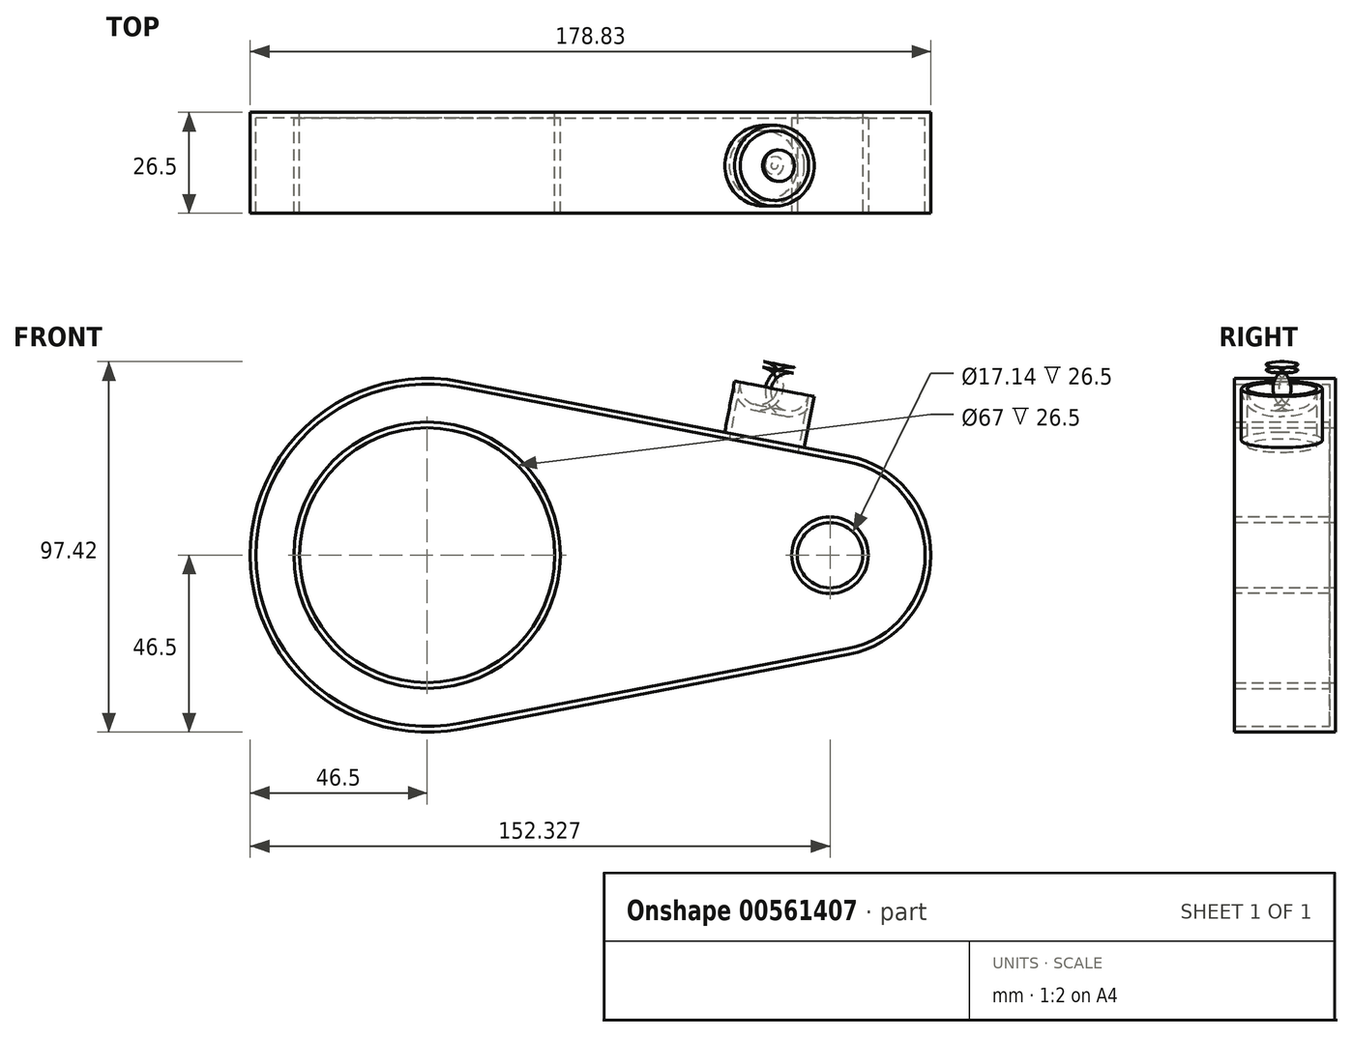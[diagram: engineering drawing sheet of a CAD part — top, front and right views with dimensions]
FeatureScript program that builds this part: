
annotation { "Feature Type Name" : "Feature", "Feature Type Description" : "" }
export const myFeature = defineFeature(function(context is Context, id is Id, definition is map)
    precondition{}
    {
        {
            var Q0;
            Q0=qCreatedBy(makeId("Front.planeOp"),FACE);
            var sketch = newSketch(context, id + "F0", { "sketchPlane" : qUnion([Q0])});
            skCircle(sketch, "E0", {"center": v(0, 0) * mm, "radius": 45 * mm});
            skCircle(sketch, "E1", {"center": v(105.83, 0) * mm, "radius": 25 * mm});
            skLineSegment(sketch, "E2", {"start": v(8.5, 44.19) * mm, "end": v(110.55, 24.55) * mm});
            skLineSegment(sketch, "E3", {"start": v(8.5, -44.19) * mm, "end": v(110.55, -24.55) * mm});
            skCircle(sketch, "E4", {"center": v(0, 0) * mm, "radius": 35 * mm});
            skSolve(sketch);
        }
        {
            var Q0;
            {var subQ0=sQuery(id+"F0.wireOp",EDGE,"E1");var subQ1=makeQuery(id+"F0.imprint","INTERSECT",VERTEX,{"derivedFrom":[subQ0,sQuery(id+"F0.wireOp",EDGE,"E2")]});Q0=makeQuery(id+"F0.imprint","IMPRINT",FACE,{"disambiguationData":[TD([[makeQuery(id+"F0.imprint","IMPRINT",EDGE,{"disambiguationData":[TD([[subQ1,-1.0]])],"derivedFrom":subQ0}),1.0]])]});}
            var Q1;
            {var subQ0=sQuery(id+"F0.wireOp",EDGE,"E2");Q1=makeQuery(id+"F0.imprint","IMPRINT",FACE,{"disambiguationData":[TD([[makeQuery(id+"F0.imprint","IMPRINT",EDGE,{"derivedFrom":subQ0}),-1.0]])]});}
            var Q2;
            Q2=makeQuery(id+"F0.imprint","IMPRINT",FACE,{"disambiguationData":[TD([[makeQuery(id+"F0.imprint","IMPRINT",EDGE,{"derivedFrom":sQuery(id+"F0.wireOp",EDGE,"E4")}),-1.0]])]});
            extrude(context, id + "F1", {"entities" : qUnion([Q0, Q1, Q2]), "depth" : 25 * mm, "offsetDistance" : 25 * mm});
        }
        {
            var Q0;
            Q0=makeQuery(id+"F1.opExtrude","SWEPT_FACE",FACE,{"disambiguationData":[OSD([sQuery(id+"F0.wireOp",EDGE,"E2")])]});
            var sketch = newSketch(context, id + "F2", { "sketchPlane" : qUnion([Q0])});
            skCircle(sketch, "E5", {"center": v(81.3, -12.5) * mm, "radius": 9.15 * mm});
            skPoint(sketch, "E5.centerSnap0", {"position": v(103.92, -12.5) * mm});
            skSolve(sketch);
        }
        {
            var Q0;
            Q0=makeQuery(id+"F2.imprint","IMPRINT",FACE,{"disambiguationData":[TD([[makeQuery(id+"F2.imprint","IMPRINT",EDGE,{"derivedFrom":sQuery(id+"F2.wireOp",EDGE,"E5")}),1.0]])]});
            extrude(context, id + "F3", {"entities" : qUnion([Q0]), "operationType" : NewBodyOperationType.ADD, "depth" : 20.2 * mm, "offsetDistance" : 25 * mm});
        }
        {
            var Q0;
            Q0=makeQuery(id+"F3.opExtrude","CAP_EDGE",EDGE,{"disambiguationData":[OSD([sQuery(id+"F2.wireOp",EDGE,"E5")])],"isStart":true});
            var Q1;
            Q1=makeQuery(id+"F3.opExtrude","CAP_EDGE",EDGE,{"disambiguationData":[OSD([sQuery(id+"F2.wireOp",EDGE,"E5")])],"isStart":false});
            fillet(context, id + "F4", {"entities" : qUnion([Q0, Q1]), "radius" : 5 * mm, "tangentPropagation" : true, "allowEdgeOverflow" : false});
        }
        {
            var Q0;
            Q0=makeQuery(id+"F1.opExtrude","CAP_FACE",FACE,{"disambiguationData":[OSD([sQuery(id+"F0.wireOp",EDGE,"E0"),sQuery(id+"F0.wireOp",EDGE,"E1"),sQuery(id+"F0.wireOp",EDGE,"E2"),sQuery(id+"F0.wireOp",EDGE,"E3"),sQuery(id+"F0.wireOp",EDGE,"E4")])],"isStart":false});
            var sketch = newSketch(context, id + "F5", { "sketchPlane" : qUnion([Q0])});
            skCircle(sketch, "E6", {"center": v(105.83, 0) * mm, "radius": 10.07 * mm});
            skSolve(sketch);
        }
        {
            var Q0;
            Q0=makeQuery(id+"F5.imprint","IMPRINT",FACE,{"disambiguationData":[TD([[makeQuery(id+"F5.imprint","IMPRINT",EDGE,{"derivedFrom":sQuery(id+"F5.wireOp",EDGE,"E6")}),1.0]])]});
            extrude(context, id + "F6", {"entities" : qUnion([Q0]), "operationType" : NewBodyOperationType.REMOVE, "endBound" : BoundingType.THROUGH_ALL, "oppositeDirection" : true, "depth" : 25 * mm, "offsetDistance" : 25 * mm});
        }
        {
            var Q0;
            Q0=makeQuery(id+"F1.opExtrude","CAP_FACE",FACE,{"disambiguationData":[OSD([sQuery(id+"F0.wireOp",EDGE,"E0"),sQuery(id+"F0.wireOp",EDGE,"E1"),sQuery(id+"F0.wireOp",EDGE,"E2"),sQuery(id+"F0.wireOp",EDGE,"E3"),sQuery(id+"F0.wireOp",EDGE,"E4")])],"isStart":false});
            shell(context, id + "F7", {"entities" : qUnion([Q0]), "thickness" : 1.5 * mm, "oppositeDirection" : true});
        }
    });
